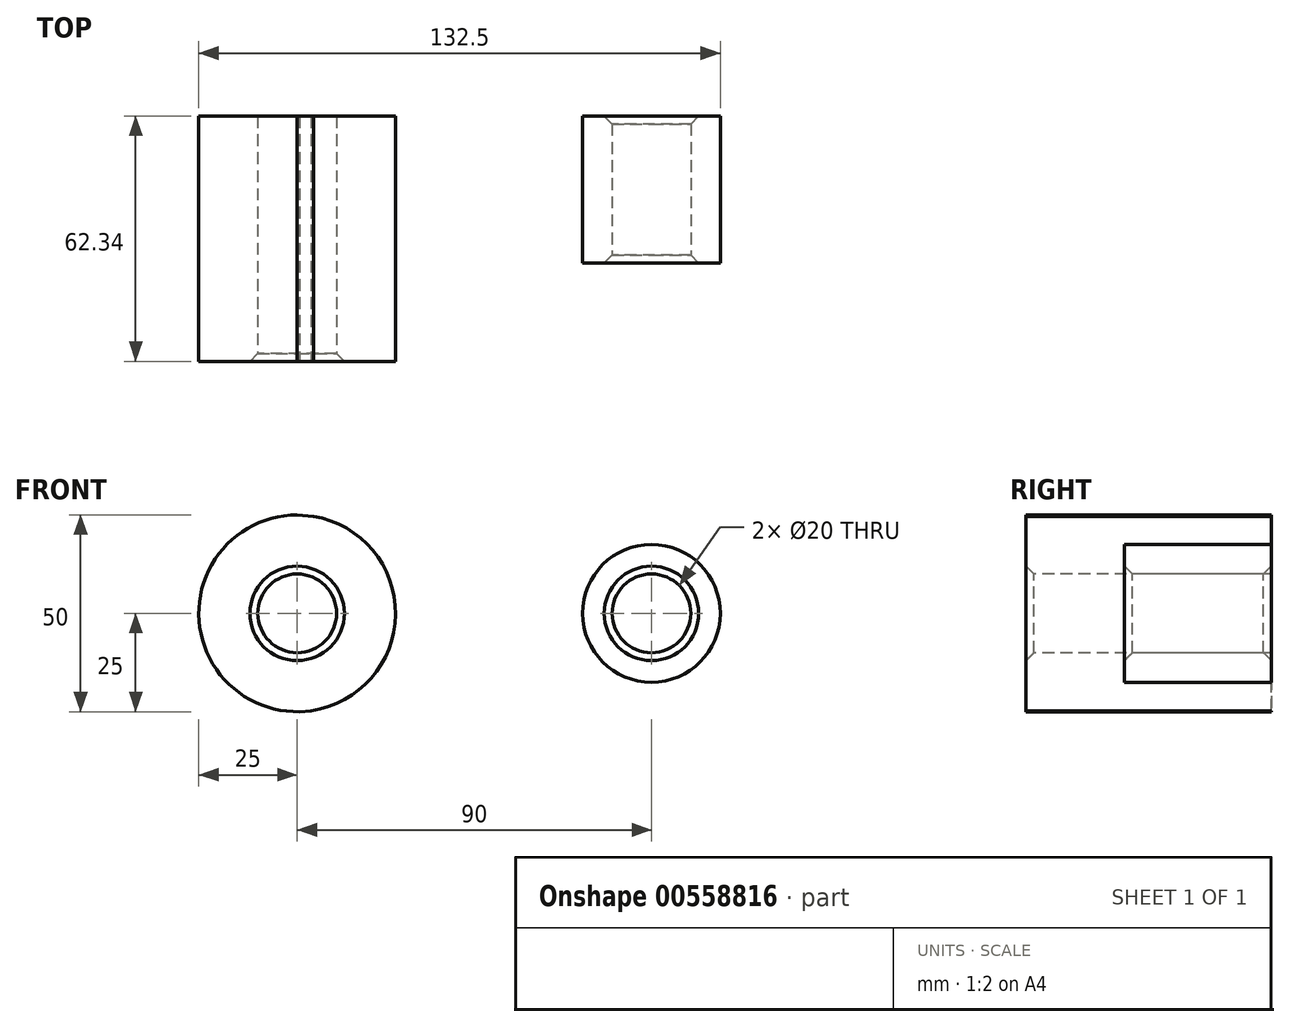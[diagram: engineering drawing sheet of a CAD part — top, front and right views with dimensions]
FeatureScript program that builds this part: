
annotation { "Feature Type Name" : "Feature", "Feature Type Description" : "" }
export const myFeature = defineFeature(function(context is Context, id is Id, definition is map)
    precondition{}
    {
        {
            var Q0;
            Q0=qCreatedBy(makeId("Front.planeOp"),FACE);
            var sketch = newSketch(context, id + "F0", { "sketchPlane" : qUnion([Q0])});
            skCircle(sketch, "E0", {"center": v(0, 0) * mm, "radius": 25 * mm});
            skCircle(sketch, "E1", {"center": v(90, 0) * mm, "radius": 17.5 * mm});
            skLineSegment(sketch, "E2", {"start": v(0, 25) * mm, "end": v(91.44, 17.44) * mm});
            skLineSegment(sketch, "E3", {"start": v(0.61, -25) * mm, "end": v(91.45, -17.44) * mm});
            skCircle(sketch, "E4", {"center": v(0, 0) * mm, "radius": 10 * mm});
            skCircle(sketch, "E5", {"center": v(90, 0) * mm, "radius": 10 * mm});
            skSolve(sketch);
        }
        {
            var Q0;
            {var subQ0=sQuery(id+"F0.wireOp",EDGE,"E2");var subQ1=sQuery(id+"F0.wireOp",EDGE,"E0");var subQ2=makeQuery(id+"F0.imprint","INTERSECT",VERTEX,{"disambiguationData":[OD(0.0)],"derivedFrom":[subQ1,subQ0]});Q0=makeQuery(id+"F0.imprint","IMPRINT",FACE,{"disambiguationData":[TD([[makeQuery(id+"F0.imprint","IMPRINT",EDGE,{"disambiguationData":[TD([[subQ2,1.0]])],"derivedFrom":subQ1}),1.0]])]});}
            var Q1;
            Q1=makeQuery(id+"F0.imprint","IMPRINT",FACE,{"disambiguationData":[TD([[makeQuery(id+"F0.imprint","IMPRINT",EDGE,{"derivedFrom":sQuery(id+"F0.wireOp",EDGE,"E4")}),-1.0]])]});
            var Q2;
            {var subQ0=sQuery(id+"F0.wireOp",EDGE,"E3");var subQ1=sQuery(id+"F0.wireOp",EDGE,"E0");var subQ2=makeQuery(id+"F0.imprint","INTERSECT",VERTEX,{"disambiguationData":[OD(0.0)],"derivedFrom":[subQ1,subQ0]});Q2=makeQuery(id+"F0.imprint","IMPRINT",FACE,{"disambiguationData":[TD([[makeQuery(id+"F0.imprint","IMPRINT",EDGE,{"disambiguationData":[TD([[subQ2,-1.0]])],"derivedFrom":subQ1}),1.0]])]});}
            var Q3;
            {var subQ0=sQuery(id+"F0.wireOp",EDGE,"E2");var subQ1=sQuery(id+"F0.wireOp",EDGE,"E0");var subQ2=makeQuery(id+"F0.imprint","INTERSECT",VERTEX,{"disambiguationData":[OD(1.0)],"derivedFrom":[subQ1,subQ0]});Q3=makeQuery(id+"F0.imprint","IMPRINT",FACE,{"disambiguationData":[TD([[makeQuery(id+"F0.imprint","IMPRINT",EDGE,{"disambiguationData":[TD([[subQ2,1.0]])],"derivedFrom":subQ1}),-1.0]])]});}
            var Q4;
            Q4=makeQuery(id+"F0.imprint","IMPRINT",FACE,{"disambiguationData":[TD([[makeQuery(id+"F0.imprint","IMPRINT",EDGE,{"derivedFrom":sQuery(id+"F0.wireOp",EDGE,"E5")}),-1.0]])]});
            extrude(context, id + "F1", {"entities" : qUnion([Q0, Q1, Q2, Q3, Q4]), "oppositeDirection" : true, "depth" : 37.34 * mm, "offsetDistance" : 25 * mm});
        }
        {
            var Q0;
            Q0=makeQuery(id+"F0.imprint","IMPRINT",FACE,{"disambiguationData":[TD([[makeQuery(id+"F0.imprint","IMPRINT",EDGE,{"derivedFrom":sQuery(id+"F0.wireOp",EDGE,"E4")}),-1.0]])]});
            extrude(context, id + "F2", {"entities" : qUnion([Q0]), "operationType" : NewBodyOperationType.ADD, "depth" : 25 * mm, "offsetDistance" : 25 * mm});
        }
        {
            var Q0;
            Q0=makeQuery(id+"F2.opExtrude","CAP_EDGE",EDGE,{"disambiguationData":[OSD([sQuery(id+"F0.wireOp",EDGE,"E4")])],"isStart":false});
            var Q1;
            {var subQ0=sQuery(id+"F0.wireOp",EDGE,"E0");Q1=makeQuery(id+"F2.opExtrude","CAP_EDGE",EDGE,{"disambiguationData":[OSD([subQ0]),TDD([makeQuery(id+"F0.imprint","IMPRINT",EDGE,{"disambiguationData":[TD([[makeQuery(id+"F0.imprint","INTERSECT",VERTEX,{"disambiguationData":[OD(1.0)],"derivedFrom":[subQ0,sQuery(id+"F0.wireOp",EDGE,"E2")]}),1.0]])],"derivedFrom":subQ0})])],"isStart":false});}
            var Q2;
            Q2=makeQuery(id+"F1.opExtrude","CAP_EDGE",EDGE,{"disambiguationData":[OSD([sQuery(id+"F0.wireOp",EDGE,"E5")])],"isStart":true});
            var Q3;
            Q3=makeQuery(id+"F1.opExtrude","CAP_EDGE",EDGE,{"disambiguationData":[OSD([sQuery(id+"F0.wireOp",EDGE,"E3")])],"isStart":true});
            chamfer(context, id + "F3", {"entities" : qUnion([Q0, Q1, Q2, Q3]), "width" : 2 * mm, "tangentPropagation" : true});
        }
        {
            var Q0;
            Q0=makeQuery(id+"F1.opExtrude","CAP_EDGE",EDGE,{"disambiguationData":[OSD([sQuery(id+"F0.wireOp",EDGE,"E4")])],"isStart":false});
            var Q1;
            Q1=makeQuery(id+"F1.opExtrude","CAP_EDGE",EDGE,{"disambiguationData":[OSD([sQuery(id+"F0.wireOp",EDGE,"E5")])],"isStart":false});
            var Q2;
            Q2=makeQuery(id+"F1.opExtrude","CAP_EDGE",EDGE,{"disambiguationData":[OSD([sQuery(id+"F0.wireOp",EDGE,"E3")])],"isStart":false});
            var Q3;
            Q3=makeQuery(id+"F1.opExtrude","CAP_EDGE",EDGE,{"disambiguationData":[OSD([sQuery(id+"F0.wireOp",EDGE,"E0")])],"isStart":false});
            chamfer(context, id + "F4", {"entities" : qUnion([Q0, Q1, Q2, Q3]), "width" : 2 * mm, "tangentPropagation" : true});
        }
    });
